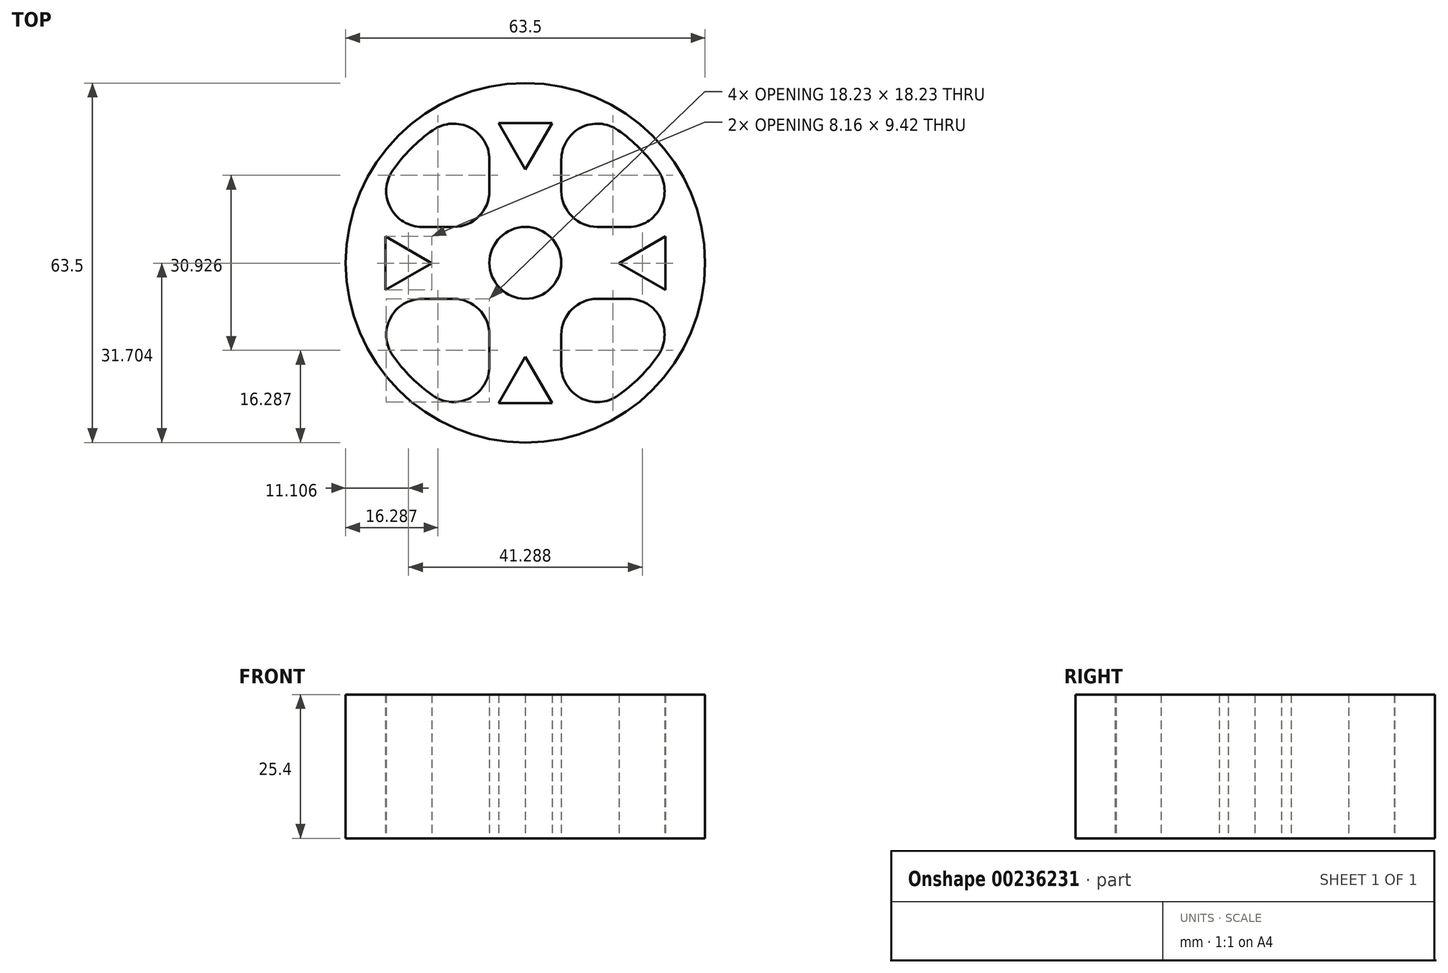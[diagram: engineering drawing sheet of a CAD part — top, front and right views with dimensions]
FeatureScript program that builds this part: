
annotation { "Feature Type Name" : "Feature", "Feature Type Description" : "" }
export const myFeature = defineFeature(function(context is Context, id is Id, definition is map)
    precondition{}
    {
        {
            var Q0;
            Q0=qCreatedBy(makeId("Top.planeOp"),FACE);
            var sketch = newSketch(context, id + "F0", { "sketchPlane" : qUnion([Q0])});
            skCircle(sketch, "E0", {"center": v(0, 0) * mm, "radius": 6.35 * mm});
            skCircle(sketch, "E1", {"center": v(0, 0) * mm, "radius": 31.75 * mm});
            skArc(sketch, "E2", {"start": v(-23.45, -16.33) * mm, "mid": v(-20.2, -20.2) * mm, "end": v(-16.33, -23.45) * mm});
            skLineSegment(sketch, "E3", {"start": v(0, 0) * mm, "end": v(0, 28.58) * mm});
            skLineSegment(sketch, "E4.0", {"start": v(6.35, 12.7) * mm, "end": v(6.35, 18.24) * mm});
            skLineSegment(sketch, "E5.0", {"start": v(-6.35, 12.7) * mm, "end": v(-6.35, 18.24) * mm});
            skLineSegment(sketch, "E6", {"start": v(0, 0) * mm, "end": v(28.58, 0) * mm});
            skLineSegment(sketch, "E7.0", {"start": v(12.7, -6.35) * mm, "end": v(18.24, -6.35) * mm});
            skLineSegment(sketch, "E8.0", {"start": v(12.7, 6.35) * mm, "end": v(18.24, 6.35) * mm});
            skLineSegment(sketch, "E9", {"start": v(0, 0) * mm, "end": v(-28.58, 0) * mm});
            skLineSegment(sketch, "E10.0", {"start": v(-12.7, 6.35) * mm, "end": v(-18.24, 6.35) * mm});
            skLineSegment(sketch, "E11.0", {"start": v(-12.7, -6.35) * mm, "end": v(-18.24, -6.35) * mm});
            skLineSegment(sketch, "E12", {"start": v(0, 0) * mm, "end": v(0, -28.58) * mm});
            skLineSegment(sketch, "E13.0", {"start": v(-6.35, -12.7) * mm, "end": v(-6.35, -18.24) * mm});
            skLineSegment(sketch, "E14.0", {"start": v(6.35, -12.7) * mm, "end": v(6.35, -18.24) * mm});
            skArc(sketch, "E15.trimOffspring", {"start": v(-16.33, 23.45) * mm, "mid": v(-20.2, 20.2) * mm, "end": v(-23.45, 16.33) * mm});
            skArc(sketch, "E16.trimOffspring", {"start": v(23.45, 16.33) * mm, "mid": v(20.2, 20.2) * mm, "end": v(16.33, 23.45) * mm});
            skArc(sketch, "E17.trimOffspring", {"start": v(16.33, -23.45) * mm, "mid": v(20.2, -20.2) * mm, "end": v(23.45, -16.33) * mm});
            skPoint(sketch, "E18.visualSharp", {"position": v(-6.35, 27.86) * mm});
            skArc(sketch, "E18.filletArc", {"start": v(-6.35, 18.24) * mm, "mid": v(-9.76, 23.87) * mm, "end": v(-16.33, 23.45) * mm});
            skPoint(sketch, "E19.visualSharp", {"position": v(-27.86, 6.35) * mm});
            skArc(sketch, "E19.filletArc", {"start": v(-23.45, 16.33) * mm, "mid": v(-23.87, 9.76) * mm, "end": v(-18.24, 6.35) * mm});
            skPoint(sketch, "E20.visualSharp", {"position": v(-6.35, 6.35) * mm});
            skArc(sketch, "E20.filletArc", {"start": v(-12.7, 6.35) * mm, "mid": v(-8.2, 8.2) * mm, "end": v(-6.35, 12.7) * mm});
            skPoint(sketch, "E21.visualSharp", {"position": v(6.35, 27.86) * mm});
            skArc(sketch, "E21.filletArc", {"start": v(16.33, 23.45) * mm, "mid": v(9.76, 23.87) * mm, "end": v(6.35, 18.24) * mm});
            skPoint(sketch, "E22.visualSharp", {"position": v(27.86, 6.35) * mm});
            skArc(sketch, "E22.filletArc", {"start": v(18.24, 6.35) * mm, "mid": v(23.87, 9.76) * mm, "end": v(23.45, 16.33) * mm});
            skPoint(sketch, "E23.visualSharp", {"position": v(6.35, 6.35) * mm});
            skArc(sketch, "E23.filletArc", {"start": v(6.35, 12.7) * mm, "mid": v(8.2, 8.2) * mm, "end": v(12.7, 6.35) * mm});
            skPoint(sketch, "E24.visualSharp", {"position": v(6.35, -6.35) * mm});
            skArc(sketch, "E24.filletArc", {"start": v(12.7, -6.35) * mm, "mid": v(8.2, -8.2) * mm, "end": v(6.35, -12.7) * mm});
            skPoint(sketch, "E25.visualSharp", {"position": v(27.86, -6.35) * mm});
            skArc(sketch, "E25.filletArc", {"start": v(23.45, -16.33) * mm, "mid": v(23.87, -9.76) * mm, "end": v(18.24, -6.35) * mm});
            skPoint(sketch, "E26.visualSharp", {"position": v(6.35, -27.86) * mm});
            skArc(sketch, "E26.filletArc", {"start": v(6.35, -18.24) * mm, "mid": v(9.76, -23.87) * mm, "end": v(16.33, -23.45) * mm});
            skPoint(sketch, "E27.visualSharp", {"position": v(-6.35, -27.86) * mm});
            skArc(sketch, "E27.filletArc", {"start": v(-16.33, -23.45) * mm, "mid": v(-9.76, -23.87) * mm, "end": v(-6.35, -18.24) * mm});
            skPoint(sketch, "E28.visualSharp", {"position": v(-27.86, -6.35) * mm});
            skArc(sketch, "E28.filletArc", {"start": v(-18.24, -6.35) * mm, "mid": v(-23.87, -9.76) * mm, "end": v(-23.45, -16.33) * mm});
            skPoint(sketch, "E29.visualSharp", {"position": v(-6.35, -6.35) * mm});
            skArc(sketch, "E29.filletArc", {"start": v(-6.35, -12.7) * mm, "mid": v(-8.2, -8.2) * mm, "end": v(-12.7, -6.35) * mm});
            skCircle(sketch, "E30.cCircle", {"center": v(0, 21.96) * mm, "radius": 2.72 * mm, "construction": true});
            skLineSegment(sketch, "E30.0", {"start": v(4.71, 24.68) * mm, "end": v(0, 16.52) * mm});
            skLineSegment(sketch, "E30.1", {"start": v(0, 16.52) * mm, "end": v(-4.71, 24.68) * mm});
            skLineSegment(sketch, "E30.2", {"start": v(-4.71, 24.68) * mm, "end": v(4.71, 24.68) * mm});
            skPoint(sketch, "E30.0.midPoint", {"position": v(2.36, 20.6) * mm});
            skLineSegment(sketch, "E31.1.0", {"start": v(-24.72, 4.66) * mm, "end": v(-16.56, -0.05) * mm});
            skLineSegment(sketch, "E31.1.1", {"start": v(-16.56, -0.05) * mm, "end": v(-24.72, -4.76) * mm});
            skLineSegment(sketch, "E31.1.2", {"start": v(-24.72, -4.76) * mm, "end": v(-24.72, 4.66) * mm});
            skLineSegment(sketch, "E31.2.0", {"start": v(-4.71, -24.77) * mm, "end": v(0, -16.61) * mm});
            skLineSegment(sketch, "E31.2.1", {"start": v(0, -16.61) * mm, "end": v(4.71, -24.77) * mm});
            skLineSegment(sketch, "E31.2.2", {"start": v(4.71, -24.77) * mm, "end": v(-4.71, -24.77) * mm});
            skLineSegment(sketch, "E31.3.0", {"start": v(24.72, -4.76) * mm, "end": v(16.56, -0.05) * mm});
            skLineSegment(sketch, "E31.3.1", {"start": v(16.56, -0.05) * mm, "end": v(24.72, 4.66) * mm});
            skLineSegment(sketch, "E31.3.2", {"start": v(24.72, 4.66) * mm, "end": v(24.72, -4.76) * mm});
            skPoint(sketch, "E31.center", {"position": v(0, -0.05) * mm});
            skSolve(sketch);
        }
        {
            var Q0;
            Q0=makeQuery(id+"F0.imprint","IMPRINT",FACE,{"disambiguationData":[TD([[makeQuery(id+"F0.imprint","IMPRINT",EDGE,{"derivedFrom":sQuery(id+"F0.wireOp",EDGE,"E1")}),1.0]])]});
            extrude(context, id + "F1", {"entities" : qUnion([Q0]), "depth" : 25.4 * mm});
        }
    });
